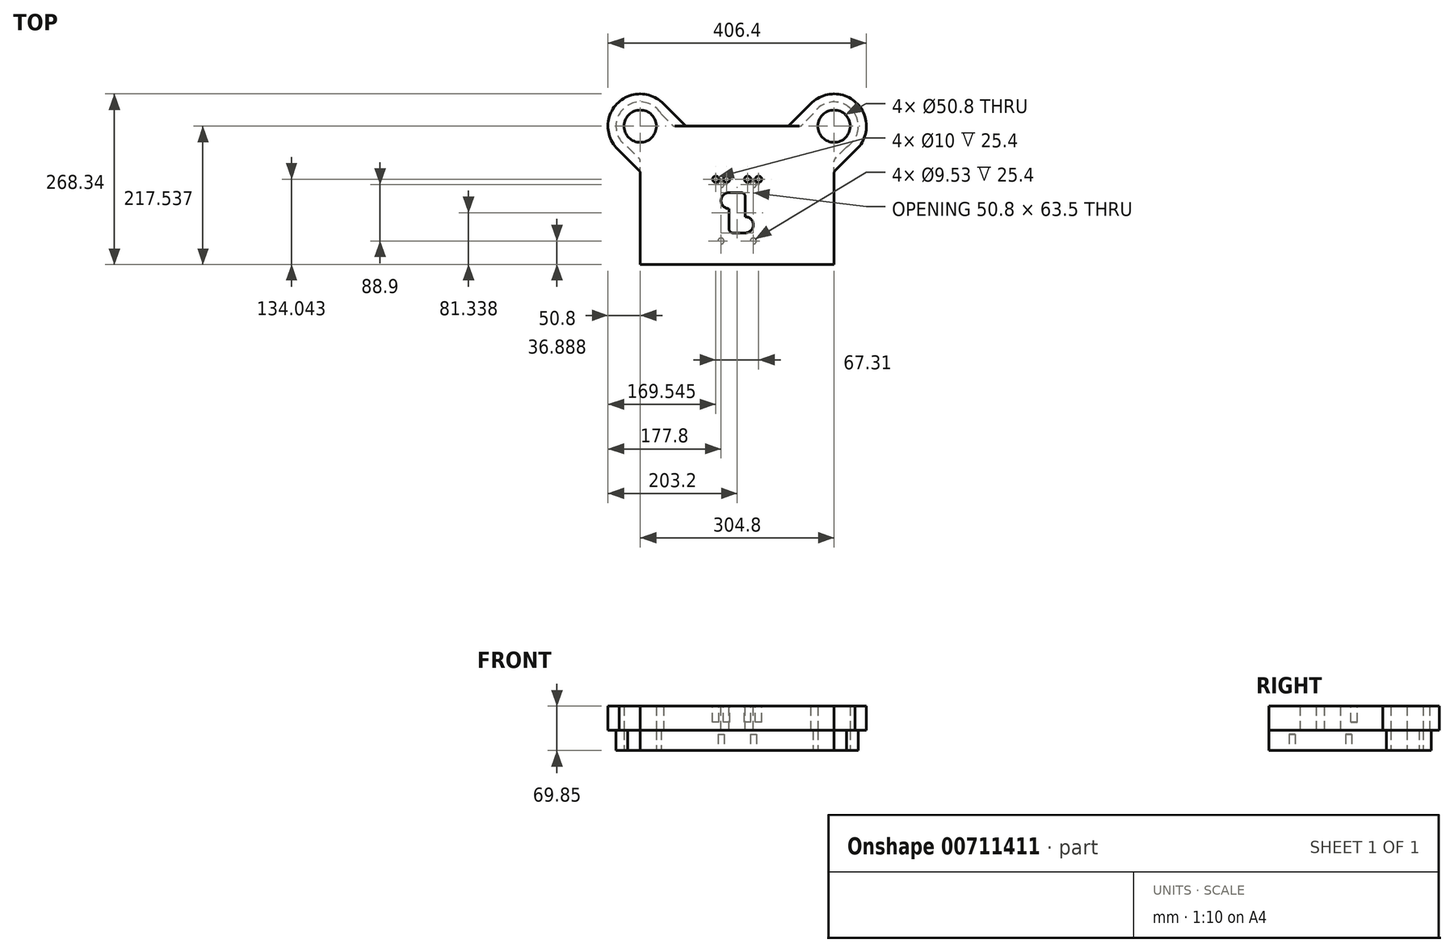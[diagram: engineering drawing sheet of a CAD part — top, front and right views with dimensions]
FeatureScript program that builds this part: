
annotation { "Feature Type Name" : "Feature", "Feature Type Description" : "" }
export const myFeature = defineFeature(function(context is Context, id is Id, definition is map)
    precondition{}
    {
        {
            var Q0;
            Q0=qCreatedBy(makeId("Top.planeOp"),FACE);
            var sketch = newSketch(context, id + "F0", { "sketchPlane" : qUnion([Q0])});
            skLineSegment(sketch, "E0.bottom", {"start": v(-152.4, -108.77) * mm, "end": v(152.4, -108.77) * mm});
            skLineSegment(sketch, "E0.top", {"start": v(-97.72, 108.77) * mm, "end": v(97.72, 108.77) * mm});
            skLineSegment(sketch, "E0.left", {"start": v(-152.4, -108.77) * mm, "end": v(-152.4, 70.67) * mm});
            skLineSegment(sketch, "E0.right", {"start": v(152.4, -108.77) * mm, "end": v(152.4, 53.9) * mm});
            skPoint(sketch, "E0.middle", {"position": v(0, 0) * mm});
            skCircle(sketch, "E1", {"center": v(-152.4, 108.77) * mm, "radius": 38.1 * mm});
            skCircle(sketch, "E2", {"center": v(152.4, 108.77) * mm, "radius": 38.1 * mm});
            skPoint(sketch, "E3", {"position": v(-119.4, 127.82) * mm});
            skPoint(sketch, "E4.MirrorP", {"position": v(119.4, 127.82) * mm});
            skLineSegment(sketch, "E5", {"start": v(-119.4, 127.82) * mm, "end": v(-102.21, 110.63) * mm});
            skLineSegment(sketch, "E6.MirrorCS", {"start": v(119.4, 127.82) * mm, "end": v(102.21, 110.63) * mm});
            skPoint(sketch, "E7.newPointB", {"position": v(100.35, 108.77) * mm});
            skArc(sketch, "E7.filletArc", {"start": v(97.72, 108.77) * mm, "mid": v(100.15, 109.25) * mm, "end": v(102.21, 110.63) * mm});
            skPoint(sketch, "E8.newPointA", {"position": v(-100.35, 108.77) * mm});
            skArc(sketch, "E8.filletArc", {"start": v(-102.21, 110.63) * mm, "mid": v(-100.15, 109.25) * mm, "end": v(-97.72, 108.77) * mm});
            skLineSegment(sketch, "E9", {"start": v(171.9, 76.04) * mm, "end": v(154.26, 58.4) * mm});
            skArc(sketch, "E10.filletArc", {"start": v(154.26, 58.4) * mm, "mid": v(152.88, 56.33) * mm, "end": v(152.4, 53.9) * mm});
            skLineSegment(sketch, "E11.MirrorCS", {"start": v(-171.9, 76.04) * mm, "end": v(-154.26, 58.4) * mm});
            skArc(sketch, "E12.MirrorCS", {"start": v(-154.26, 58.4) * mm, "mid": v(-152.88, 56.33) * mm, "end": v(-152.4, 53.9) * mm});
            skCircle(sketch, "E13", {"center": v(-152.4, 108.77) * mm, "radius": 25.4 * mm});
            skCircle(sketch, "E14", {"center": v(152.4, 108.77) * mm, "radius": 25.4 * mm});
            skSolve(sketch);
        }
        {
            var Q0;
            {var subQ7=sQuery(id+"F0.wireOp",EDGE,"E0.bottom");Q0=makeQuery(id+"F0.imprint","IMPRINT",FACE,{"disambiguationData":[TD([[makeQuery(id+"F0.imprint","IMPRINT",EDGE,{"derivedFrom":subQ7}),1.0]])]});}
            var Q1;
            Q1=makeQuery(id+"F0.imprint","IMPRINT",FACE,{"disambiguationData":[TD([[makeQuery(id+"F0.imprint","IMPRINT",EDGE,{"derivedFrom":sQuery(id+"F0.wireOp",EDGE,"E13")}),-1.0]])]});
            var Q2;
            Q2=makeQuery(id+"F0.imprint","IMPRINT",FACE,{"disambiguationData":[TD([[makeQuery(id+"F0.imprint","IMPRINT",EDGE,{"derivedFrom":sQuery(id+"F0.wireOp",EDGE,"E14")}),-1.0]])]});
            var Q3;
            {var subQ4=sQuery(id+"F0.wireOp",EDGE,"E11.MirrorCS");Q3=makeQuery(id+"F0.imprint","IMPRINT",FACE,{"disambiguationData":[TD([[makeQuery(id+"F0.imprint","IMPRINT",EDGE,{"derivedFrom":subQ4}),1.0]])]});}
            extrude(context, id + "F1", {"entities" : qUnion([Q0, Q1, Q2, Q3]), "depth" : 31.75 * mm, "offsetDistance" : 25.4 * mm});
        }
        {
            var Q0;
            Q0=makeQuery(id+"F1.opExtrude","SWEPT_BODY",BODY,{"disambiguationData":[OSD([sQuery(id+"F0.wireOp",EDGE,"E0.bottom"),sQuery(id+"F0.wireOp",EDGE,"E0.top"),sQuery(id+"F0.wireOp",EDGE,"E0.left"),sQuery(id+"F0.wireOp",EDGE,"E0.right"),sQuery(id+"F0.wireOp",EDGE,"E1"),sQuery(id+"F0.wireOp",EDGE,"E2"),sQuery(id+"F0.wireOp",EDGE,"E5"),sQuery(id+"F0.wireOp",EDGE,"E6.MirrorCS"),sQuery(id+"F0.wireOp",EDGE,"E7.filletArc"),sQuery(id+"F0.wireOp",EDGE,"E8.filletArc"),sQuery(id+"F0.wireOp",EDGE,"E9"),sQuery(id+"F0.wireOp",EDGE,"E10.filletArc"),sQuery(id+"F0.wireOp",EDGE,"E11.MirrorCS"),sQuery(id+"F0.wireOp",EDGE,"E12.MirrorCS"),sQuery(id+"F0.wireOp",EDGE,"E13"),sQuery(id+"F0.wireOp",EDGE,"E14")])]});
            transform(context, id + "F2", {"entities" : qUnion([Q0]), "transformType" : TransformType.TRANSLATION_3D, "dx" : 0 * mm, "dy" : 0 * mm, "dz" : 0 * mm, "makeCopy" : true});
        }
        {
            var Q0;
            Q0=makeQuery(id+"F2.opPattern","COPY",BODY,{"derivedFrom":makeQuery(id+"F1.opExtrude","SWEPT_BODY",BODY,{"disambiguationData":[OSD([sQuery(id+"F0.wireOp",EDGE,"E0.bottom"),sQuery(id+"F0.wireOp",EDGE,"E0.top"),sQuery(id+"F0.wireOp",EDGE,"E0.left"),sQuery(id+"F0.wireOp",EDGE,"E0.right"),sQuery(id+"F0.wireOp",EDGE,"E1"),sQuery(id+"F0.wireOp",EDGE,"E2"),sQuery(id+"F0.wireOp",EDGE,"E5"),sQuery(id+"F0.wireOp",EDGE,"E6.MirrorCS"),sQuery(id+"F0.wireOp",EDGE,"E7.filletArc"),sQuery(id+"F0.wireOp",EDGE,"E8.filletArc"),sQuery(id+"F0.wireOp",EDGE,"E9"),sQuery(id+"F0.wireOp",EDGE,"E10.filletArc"),sQuery(id+"F0.wireOp",EDGE,"E11.MirrorCS"),sQuery(id+"F0.wireOp",EDGE,"E12.MirrorCS"),sQuery(id+"F0.wireOp",EDGE,"E13"),sQuery(id+"F0.wireOp",EDGE,"E14")])]}),"instanceName":"1"});
            deleteBodies(context, id + "F3", {"entities" : qUnion([Q0])});
        }
        {
            var Q0;
            Q0=makeQuery(id+"F1.opExtrude","CAP_FACE",FACE,{"disambiguationData":[OSD([sQuery(id+"F0.wireOp",EDGE,"E0.bottom"),sQuery(id+"F0.wireOp",EDGE,"E0.top"),sQuery(id+"F0.wireOp",EDGE,"E0.left"),sQuery(id+"F0.wireOp",EDGE,"E0.right"),sQuery(id+"F0.wireOp",EDGE,"E1"),sQuery(id+"F0.wireOp",EDGE,"E2"),sQuery(id+"F0.wireOp",EDGE,"E5"),sQuery(id+"F0.wireOp",EDGE,"E6.MirrorCS"),sQuery(id+"F0.wireOp",EDGE,"E7.filletArc"),sQuery(id+"F0.wireOp",EDGE,"E8.filletArc"),sQuery(id+"F0.wireOp",EDGE,"E9"),sQuery(id+"F0.wireOp",EDGE,"E10.filletArc"),sQuery(id+"F0.wireOp",EDGE,"E11.MirrorCS"),sQuery(id+"F0.wireOp",EDGE,"E12.MirrorCS"),sQuery(id+"F0.wireOp",EDGE,"E13"),sQuery(id+"F0.wireOp",EDGE,"E14")])],"isStart":false});
            var sketch = newSketch(context, id + "F4", { "sketchPlane" : qUnion([Q0])});
            skCircle(sketch, "E15", {"center": v(-152.4, 108.77) * mm, "radius": 25.4 * mm});
            skCircle(sketch, "E16", {"center": v(152.4, 108.77) * mm, "radius": 25.4 * mm});
            skLineSegment(sketch, "E17.bottom", {"start": v(152.4, -108.77) * mm, "end": v(-152.4, -108.77) * mm});
            skLineSegment(sketch, "E17.top", {"start": v(77.94, 108.77) * mm, "end": v(-77.94, 108.77) * mm});
            skLineSegment(sketch, "E17.left", {"start": v(152.4, -108.77) * mm, "end": v(152.4, 34.49) * mm});
            skLineSegment(sketch, "E17.right", {"start": v(-152.4, -108.77) * mm, "end": v(-152.4, 34.49) * mm});
            skPoint(sketch, "E17.middle", {"position": v(0, 0) * mm});
            skArc(sketch, "E18", {"start": v(-115.71, 143.9) * mm, "mid": v(-189.24, 143.75) * mm, "end": v(-185.6, 70.31) * mm});
            skArc(sketch, "E19", {"start": v(185.6, 70.31) * mm, "mid": v(189.24, 143.75) * mm, "end": v(115.71, 143.9) * mm});
            skLineSegment(sketch, "E20", {"start": v(-117.26, 145.46) * mm, "end": v(-82.43, 110.63) * mm});
            skArc(sketch, "E21.filletArc", {"start": v(-82.43, 110.63) * mm, "mid": v(-80.37, 109.25) * mm, "end": v(-77.94, 108.77) * mm});
            skLineSegment(sketch, "E22.MirrorCS", {"start": v(117.26, 145.46) * mm, "end": v(82.43, 110.63) * mm});
            skArc(sketch, "E23.MirrorCS", {"start": v(82.43, 110.63) * mm, "mid": v(80.37, 109.25) * mm, "end": v(77.94, 108.77) * mm});
            skLineSegment(sketch, "E24", {"start": v(-190.85, 75.57) * mm, "end": v(-154.26, 38.98) * mm});
            skArc(sketch, "E25.filletArc", {"start": v(-152.4, 34.49) * mm, "mid": v(-152.88, 36.92) * mm, "end": v(-154.26, 38.98) * mm});
            skLineSegment(sketch, "E26.MirrorCS", {"start": v(190.85, 75.57) * mm, "end": v(154.26, 38.98) * mm});
            skArc(sketch, "E27.MirrorCS", {"start": v(152.4, 34.49) * mm, "mid": v(152.88, 36.92) * mm, "end": v(154.26, 38.98) * mm});
            skSolve(sketch);
        }
        {
            var Q0;
            Q0=qSketchRegion(id+"F4",true);
            extrude(context, id + "F5", {"entities" : qUnion([Q0]), "depth" : 38.1 * mm, "offsetDistance" : 25.4 * mm});
        }
        {
            var Q0;
            Q0=makeQuery(id+"F1.opExtrude","CAP_FACE",FACE,{"disambiguationData":[OSD([sQuery(id+"F0.wireOp",EDGE,"E0.bottom"),sQuery(id+"F0.wireOp",EDGE,"E0.top"),sQuery(id+"F0.wireOp",EDGE,"E0.left"),sQuery(id+"F0.wireOp",EDGE,"E0.right"),sQuery(id+"F0.wireOp",EDGE,"E1"),sQuery(id+"F0.wireOp",EDGE,"E2"),sQuery(id+"F0.wireOp",EDGE,"E5"),sQuery(id+"F0.wireOp",EDGE,"E6.MirrorCS"),sQuery(id+"F0.wireOp",EDGE,"E7.filletArc"),sQuery(id+"F0.wireOp",EDGE,"E8.filletArc"),sQuery(id+"F0.wireOp",EDGE,"E9"),sQuery(id+"F0.wireOp",EDGE,"E10.filletArc"),sQuery(id+"F0.wireOp",EDGE,"E11.MirrorCS"),sQuery(id+"F0.wireOp",EDGE,"E12.MirrorCS"),sQuery(id+"F0.wireOp",EDGE,"E13"),sQuery(id+"F0.wireOp",EDGE,"E14")])],"isStart":true});
            var sketch = newSketch(context, id + "F6", { "sketchPlane" : qUnion([Q0])});
            skLineSegment(sketch, "E28", {"start": v(-152.4, 27.43) * mm, "end": v(152.4, 27.43) * mm});
            skLineSegment(sketch, "E29", {"start": v(0, 108.77) * mm, "end": v(0, -108.77) * mm});
            skLineSegment(sketch, "E30.bottom", {"start": v(25.4, -17.02) * mm, "end": v(-25.4, -17.02) * mm});
            skLineSegment(sketch, "E30.top", {"start": v(25.4, 71.88) * mm, "end": v(-25.4, 71.88) * mm});
            skLineSegment(sketch, "E30.left", {"start": v(25.4, -17.02) * mm, "end": v(25.4, 71.88) * mm});
            skLineSegment(sketch, "E30.right", {"start": v(-25.4, -17.02) * mm, "end": v(-25.4, 71.88) * mm});
            skPoint(sketch, "E30.middle", {"position": v(0, 27.43) * mm});
            skCircle(sketch, "E31", {"center": v(-25.4, 71.88) * mm, "radius": 4.76 * mm});
            skCircle(sketch, "E32", {"center": v(25.4, 71.88) * mm, "radius": 4.76 * mm});
            skCircle(sketch, "E33", {"center": v(25.4, -17.02) * mm, "radius": 4.76 * mm});
            skCircle(sketch, "E34", {"center": v(-25.4, -17.02) * mm, "radius": 4.76 * mm});
            skSolve(sketch);
        }
        {
            var Q0;
            {var subQ0=sQuery(id+"F6.wireOp",EDGE,"E30.right");var subQ1=sQuery(id+"F6.wireOp",EDGE,"E30.top");var subQ2=makeQuery(id+"F6.imprint","INTERSECT",VERTEX,{"derivedFrom":[subQ1,subQ0]});Q0=makeQuery(id+"F6.imprint","IMPRINT",FACE,{"disambiguationData":[TD([[makeQuery(id+"F6.imprint","IMPRINT",EDGE,{"disambiguationData":[TD([[subQ2,1.0]])],"derivedFrom":subQ1}),1.0]])]});}
            var Q1;
            {var subQ0=sQuery(id+"F6.wireOp",EDGE,"E30.right");var subQ1=sQuery(id+"F6.wireOp",EDGE,"E30.top");var subQ2=makeQuery(id+"F6.imprint","INTERSECT",VERTEX,{"derivedFrom":[subQ1,subQ0]});Q1=makeQuery(id+"F6.imprint","IMPRINT",FACE,{"disambiguationData":[TD([[makeQuery(id+"F6.imprint","IMPRINT",EDGE,{"disambiguationData":[TD([[subQ2,1.0]])],"derivedFrom":subQ1}),-1.0]])]});}
            var Q2;
            {var subQ0=sQuery(id+"F6.wireOp",EDGE,"E30.left");var subQ1=sQuery(id+"F6.wireOp",EDGE,"E30.top");var subQ2=makeQuery(id+"F6.imprint","INTERSECT",VERTEX,{"derivedFrom":[subQ1,subQ0]});Q2=makeQuery(id+"F6.imprint","IMPRINT",FACE,{"disambiguationData":[TD([[makeQuery(id+"F6.imprint","IMPRINT",EDGE,{"disambiguationData":[TD([[subQ2,-1.0]])],"derivedFrom":subQ1}),-1.0]])]});}
            var Q3;
            {var subQ0=sQuery(id+"F6.wireOp",EDGE,"E30.left");var subQ1=sQuery(id+"F6.wireOp",EDGE,"E30.top");var subQ2=makeQuery(id+"F6.imprint","INTERSECT",VERTEX,{"derivedFrom":[subQ1,subQ0]});Q3=makeQuery(id+"F6.imprint","IMPRINT",FACE,{"disambiguationData":[TD([[makeQuery(id+"F6.imprint","IMPRINT",EDGE,{"disambiguationData":[TD([[subQ2,-1.0]])],"derivedFrom":subQ1}),1.0]])]});}
            var Q4;
            {var subQ0=sQuery(id+"F6.wireOp",EDGE,"E30.right");var subQ1=sQuery(id+"F6.wireOp",EDGE,"E30.bottom");var subQ2=makeQuery(id+"F6.imprint","INTERSECT",VERTEX,{"derivedFrom":[subQ1,subQ0]});Q4=makeQuery(id+"F6.imprint","IMPRINT",FACE,{"disambiguationData":[TD([[makeQuery(id+"F6.imprint","IMPRINT",EDGE,{"disambiguationData":[TD([[subQ2,1.0]])],"derivedFrom":subQ1}),-1.0]])]});}
            var Q5;
            {var subQ0=sQuery(id+"F6.wireOp",EDGE,"E30.right");var subQ1=sQuery(id+"F6.wireOp",EDGE,"E30.bottom");var subQ2=makeQuery(id+"F6.imprint","INTERSECT",VERTEX,{"derivedFrom":[subQ1,subQ0]});Q5=makeQuery(id+"F6.imprint","IMPRINT",FACE,{"disambiguationData":[TD([[makeQuery(id+"F6.imprint","IMPRINT",EDGE,{"disambiguationData":[TD([[subQ2,1.0]])],"derivedFrom":subQ1}),1.0]])]});}
            var Q6;
            {var subQ0=sQuery(id+"F6.wireOp",EDGE,"E30.left");var subQ1=sQuery(id+"F6.wireOp",EDGE,"E30.bottom");var subQ2=makeQuery(id+"F6.imprint","INTERSECT",VERTEX,{"derivedFrom":[subQ1,subQ0]});Q6=makeQuery(id+"F6.imprint","IMPRINT",FACE,{"disambiguationData":[TD([[makeQuery(id+"F6.imprint","IMPRINT",EDGE,{"disambiguationData":[TD([[subQ2,-1.0]])],"derivedFrom":subQ1}),-1.0]])]});}
            var Q7;
            {var subQ0=sQuery(id+"F6.wireOp",EDGE,"E30.left");var subQ1=sQuery(id+"F6.wireOp",EDGE,"E30.bottom");var subQ2=makeQuery(id+"F6.imprint","INTERSECT",VERTEX,{"derivedFrom":[subQ1,subQ0]});Q7=makeQuery(id+"F6.imprint","IMPRINT",FACE,{"disambiguationData":[TD([[makeQuery(id+"F6.imprint","IMPRINT",EDGE,{"disambiguationData":[TD([[subQ2,-1.0]])],"derivedFrom":subQ1}),1.0]])]});}
            extrude(context, id + "F7", {"entities" : qUnion([Q0, Q1, Q2, Q3, Q4, Q5, Q6, Q7]), "operationType" : NewBodyOperationType.REMOVE, "depth" : -25.4 * mm, "offsetDistance" : 25.4 * mm});
        }
        {
            var Q0;
            Q0=makeQuery(id+"F5.opExtrude","CAP_FACE",FACE,{"disambiguationData":[OSD([sQuery(id+"F4.wireOp",EDGE,"E15"),sQuery(id+"F4.wireOp",EDGE,"E16"),sQuery(id+"F4.wireOp",EDGE,"E17.bottom"),sQuery(id+"F4.wireOp",EDGE,"E17.top"),sQuery(id+"F4.wireOp",EDGE,"E17.left"),sQuery(id+"F4.wireOp",EDGE,"E17.right"),sQuery(id+"F4.wireOp",EDGE,"E18"),sQuery(id+"F4.wireOp",EDGE,"E19"),sQuery(id+"F4.wireOp",EDGE,"E20"),sQuery(id+"F4.wireOp",EDGE,"E21.filletArc"),sQuery(id+"F4.wireOp",EDGE,"E22.MirrorCS"),sQuery(id+"F4.wireOp",EDGE,"E23.MirrorCS"),sQuery(id+"F4.wireOp",EDGE,"E24"),sQuery(id+"F4.wireOp",EDGE,"E25.filletArc"),sQuery(id+"F4.wireOp",EDGE,"E26.MirrorCS"),sQuery(id+"F4.wireOp",EDGE,"E27.MirrorCS")])],"isStart":false});
            var sketch = newSketch(context, id + "F8", { "sketchPlane" : qUnion([Q0])});
            skLineSegment(sketch, "E35.0", {"start": v(-152.4, -108.77) * mm, "end": v(152.4, -108.77) * mm});
            skLineSegment(sketch, "E36", {"start": v(-152.4, -27.43) * mm, "end": v(152.4, -27.43) * mm});
            skLineSegment(sketch, "E37", {"start": v(0, -108.77) * mm, "end": v(0, -27.43) * mm});
            skLineSegment(sketch, "E38.bottom", {"start": v(12.7, -59.18) * mm, "end": v(-6.35, -59.18) * mm});
            skLineSegment(sketch, "E38.top", {"start": v(6.35, 4.32) * mm, "end": v(-12.7, 4.32) * mm});
            skLineSegment(sketch, "E38.right", {"start": v(-12.7, -52.83) * mm, "end": v(-12.7, -21.08) * mm});
            skPoint(sketch, "E38.middle", {"position": v(0, -27.43) * mm});
            skArc(sketch, "E39", {"start": v(-12.7, 4.32) * mm, "mid": v(-25.4, -8.38) * mm, "end": v(-12.7, -21.08) * mm});
            skArc(sketch, "E40", {"start": v(12.7, -59.18) * mm, "mid": v(25.4, -46.48) * mm, "end": v(12.7, -33.78) * mm});
            skLineSegment(sketch, "E41.trimOffspring", {"start": v(12.7, -33.78) * mm, "end": v(12.7, -2.03) * mm});
            skPoint(sketch, "E42.visualSharp", {"position": v(-12.7, -59.18) * mm});
            skArc(sketch, "E42.filletArc", {"start": v(-12.7, -52.83) * mm, "mid": v(-10.84, -57.32) * mm, "end": v(-6.35, -59.18) * mm});
            skPoint(sketch, "E43.visualSharp", {"position": v(12.7, 4.32) * mm});
            skArc(sketch, "E43.filletArc", {"start": v(12.7, -2.03) * mm, "mid": v(10.84, 2.46) * mm, "end": v(6.35, 4.32) * mm});
            skLineSegment(sketch, "E44.bottom", {"start": v(0, -46.48) * mm, "end": v(-6.35, -46.48) * mm});
            skLineSegment(sketch, "E44.top", {"start": v(0, -8.38) * mm, "end": v(-6.35, -8.38) * mm});
            skLineSegment(sketch, "E44.left", {"start": v(6.35, -40.13) * mm, "end": v(6.35, -14.73) * mm});
            skLineSegment(sketch, "E44.right", {"start": v(-6.35, -46.48) * mm, "end": v(-6.35, -8.38) * mm});
            skPoint(sketch, "E45.visualSharp", {"position": v(6.35, -8.38) * mm});
            skArc(sketch, "E45.filletArc", {"start": v(6.35, -14.73) * mm, "mid": v(4.5, -10.24) * mm, "end": v(0, -8.38) * mm});
            skPoint(sketch, "E46.visualSharp", {"position": v(6.35, -46.48) * mm});
            skArc(sketch, "E46.filletArc", {"start": v(0, -46.48) * mm, "mid": v(4.5, -44.62) * mm, "end": v(6.35, -40.13) * mm});
            skLineSegment(sketch, "E47.top", {"start": v(50.8, -78.23) * mm, "end": v(-50.8, -78.23) * mm});
            skLineSegment(sketch, "E48.top", {"start": v(-50.8, 42.42) * mm, "end": v(50.8, 42.42) * mm});
            skLineSegment(sketch, "E49", {"start": v(48.99, -50.93) * mm, "end": v(48.99, -50.93) * mm});
            skLineSegment(sketch, "E50", {"start": v(-52.61, -50.93) * mm, "end": v(-52.61, -50.93) * mm});
            skCircle(sketch, "E51", {"center": v(-33.66, 25.27) * mm, "radius": 5 * mm});
            skCircle(sketch, "E52", {"center": v(-16.51, 25.27) * mm, "radius": 5 * mm});
            skCircle(sketch, "E53", {"center": v(16.5, 25.27) * mm, "radius": 5 * mm});
            skCircle(sketch, "E54", {"center": v(33.65, 25.27) * mm, "radius": 5 * mm});
            skLineSegment(sketch, "E55.top", {"start": v(127, 10.67) * mm, "end": v(63.5, 10.67) * mm});
            skLineSegment(sketch, "E55.left", {"start": v(127, -65.53) * mm, "end": v(127, 10.67) * mm});
            skLineSegment(sketch, "E55.right", {"start": v(-127, -65.53) * mm, "end": v(-127, 10.67) * mm});
            skLineSegment(sketch, "E56.trimOffspring", {"start": v(-63.5, 10.67) * mm, "end": v(-127, 10.67) * mm});
            skLineSegment(sketch, "E57", {"start": v(-50.8, 42.42) * mm, "end": v(-50.8, 23.37) * mm});
            skLineSegment(sketch, "E58", {"start": v(50.8, 42.42) * mm, "end": v(50.8, 23.37) * mm});
            skPoint(sketch, "E59.visualSharp", {"position": v(-50.8, 10.67) * mm});
            skArc(sketch, "E59.filletArc", {"start": v(-63.5, 10.67) * mm, "mid": v(-54.52, 14.39) * mm, "end": v(-50.8, 23.37) * mm});
            skPoint(sketch, "E60.visualSharp", {"position": v(50.8, 10.67) * mm});
            skArc(sketch, "E60.filletArc", {"start": v(50.8, 23.37) * mm, "mid": v(54.52, 14.39) * mm, "end": v(63.5, 10.67) * mm});
            skLineSegment(sketch, "E61.top", {"start": v(-127, -78.23) * mm, "end": v(-50.8, -78.23) * mm});
            skLineSegment(sketch, "E61.left", {"start": v(-127, -65.53) * mm, "end": v(-127, -78.23) * mm});
            skLineSegment(sketch, "E62.bottom", {"start": v(50.8, -78.23) * mm, "end": v(127, -78.23) * mm});
            skLineSegment(sketch, "E62.right", {"start": v(127, -78.23) * mm, "end": v(127, -65.53) * mm});
            skLineSegment(sketch, "E63", {"start": v(-45.75, 10.03) * mm, "end": v(40.3, 10.03) * mm, "construction": true});
            skLineSegment(sketch, "E64", {"start": v(-126.28, -66.17) * mm, "end": v(126.43, -66.17) * mm, "construction": true});
            skCircle(sketch, "E65", {"center": v(34.17, -68.55) * mm, "radius": 2.38 * mm});
            skLineSegment(sketch, "E66", {"start": v(34.17, -68.55) * mm, "end": v(124.12, -68.55) * mm});
            skLineSegment(sketch, "E67", {"start": v(34.17, -68.55) * mm, "end": v(-125.44, -68.55) * mm});
            skCircle(sketch, "E68", {"center": v(-29.33, -68.55) * mm, "radius": 2.38 * mm});
            skCircle(sketch, "E69.1.0.0", {"center": v(-84.2, -68.55) * mm, "radius": 2.38 * mm});
            skCircle(sketch, "E70.2.0.0", {"center": v(84.97, -68.55) * mm, "radius": 2.38 * mm});
            skLineSegment(sketch, "E70.direction1", {"start": v(34.17, -68.55) * mm, "end": v(59.57, -68.55) * mm, "construction": true});
            skSolve(sketch);
        }
        {
            var Q0;
            Q0=makeQuery(id+"F8.imprint","IMPRINT",FACE,{"disambiguationData":[TD([[makeQuery(id+"F8.imprint","IMPRINT",EDGE,{"derivedFrom":sQuery(id+"F8.wireOp",EDGE,"E48.top")}),1.0]])]});
            var sketch = newSketch(context, id + "F9", { "sketchPlane" : qUnion([Q0])});
            skCircle(sketch, "E71.0", {"center": v(-33.66, 25.27) * mm, "radius": 5 * mm});
            skCircle(sketch, "E72.0", {"center": v(-16.51, 25.27) * mm, "radius": 5 * mm});
            skCircle(sketch, "E73.0", {"center": v(16.5, 25.27) * mm, "radius": 5 * mm});
            skCircle(sketch, "E74.0", {"center": v(33.65, 25.27) * mm, "radius": 5 * mm});
            skSolve(sketch);
        }
        {
            var Q0;
            Q0=makeQuery(id+"F9.imprint","IMPRINT",FACE,{"disambiguationData":[TD([[makeQuery(id+"F9.imprint","IMPRINT",EDGE,{"derivedFrom":sQuery(id+"F9.wireOp",EDGE,"E71.0")}),1.0]])]});
            var Q1;
            Q1=makeQuery(id+"F9.imprint","IMPRINT",FACE,{"disambiguationData":[TD([[makeQuery(id+"F9.imprint","IMPRINT",EDGE,{"derivedFrom":sQuery(id+"F9.wireOp",EDGE,"E72.0")}),1.0]])]});
            var Q2;
            Q2=makeQuery(id+"F9.imprint","IMPRINT",FACE,{"disambiguationData":[TD([[makeQuery(id+"F9.imprint","IMPRINT",EDGE,{"derivedFrom":sQuery(id+"F9.wireOp",EDGE,"E73.0")}),1.0]])]});
            var Q3;
            Q3=makeQuery(id+"F9.imprint","IMPRINT",FACE,{"disambiguationData":[TD([[makeQuery(id+"F9.imprint","IMPRINT",EDGE,{"derivedFrom":sQuery(id+"F9.wireOp",EDGE,"E74.0")}),1.0]])]});
            extrude(context, id + "F10", {"entities" : qUnion([Q0, Q1, Q2, Q3]), "operationType" : NewBodyOperationType.REMOVE, "oppositeDirection" : true, "depth" : 25.4 * mm, "offsetDistance" : 25.4 * mm});
        }
        {
            var Q0;
            Q0=makeQuery(id+"F8.imprint","IMPRINT",FACE,{"disambiguationData":[TD([[makeQuery(id+"F8.imprint","IMPRINT",EDGE,{"derivedFrom":sQuery(id+"F8.wireOp",EDGE,"E38.top")}),1.0]])]});
            var sketch = newSketch(context, id + "F11", { "sketchPlane" : qUnion([Q0])});
            skLineSegment(sketch, "E75.0", {"start": v(12.7, -33.78) * mm, "end": v(12.7, -2.03) * mm});
            skArc(sketch, "E76.0", {"start": v(12.7, -2.03) * mm, "mid": v(10.84, 2.46) * mm, "end": v(6.35, 4.32) * mm});
            skLineSegment(sketch, "E77.0", {"start": v(6.35, 4.32) * mm, "end": v(-12.7, 4.32) * mm});
            skArc(sketch, "E78.0", {"start": v(-12.7, 4.32) * mm, "mid": v(-25.4, -8.38) * mm, "end": v(-12.7, -21.08) * mm});
            skLineSegment(sketch, "E79.0", {"start": v(-12.7, -52.83) * mm, "end": v(-12.7, -21.08) * mm});
            skArc(sketch, "E80.0", {"start": v(-12.7, -52.83) * mm, "mid": v(-10.84, -57.32) * mm, "end": v(-6.35, -59.18) * mm});
            skLineSegment(sketch, "E81.0", {"start": v(12.7, -59.18) * mm, "end": v(-6.35, -59.18) * mm});
            skArc(sketch, "E82.0", {"start": v(12.7, -59.18) * mm, "mid": v(25.4, -46.48) * mm, "end": v(12.7, -33.78) * mm});
            skSolve(sketch);
        }
        {
            var Q0;
            Q0 = qSketchRegion(id + "F11", true);
            extrude(context, id + "F12", {"entities" : qUnion([Q0]), "operationType" : NewBodyOperationType.REMOVE, "endBound" : BoundingType.UP_TO_NEXT, "oppositeDirection" : true, "depth" : 25.4 * mm, "offsetDistance" : 25.4 * mm});
        }
    });
